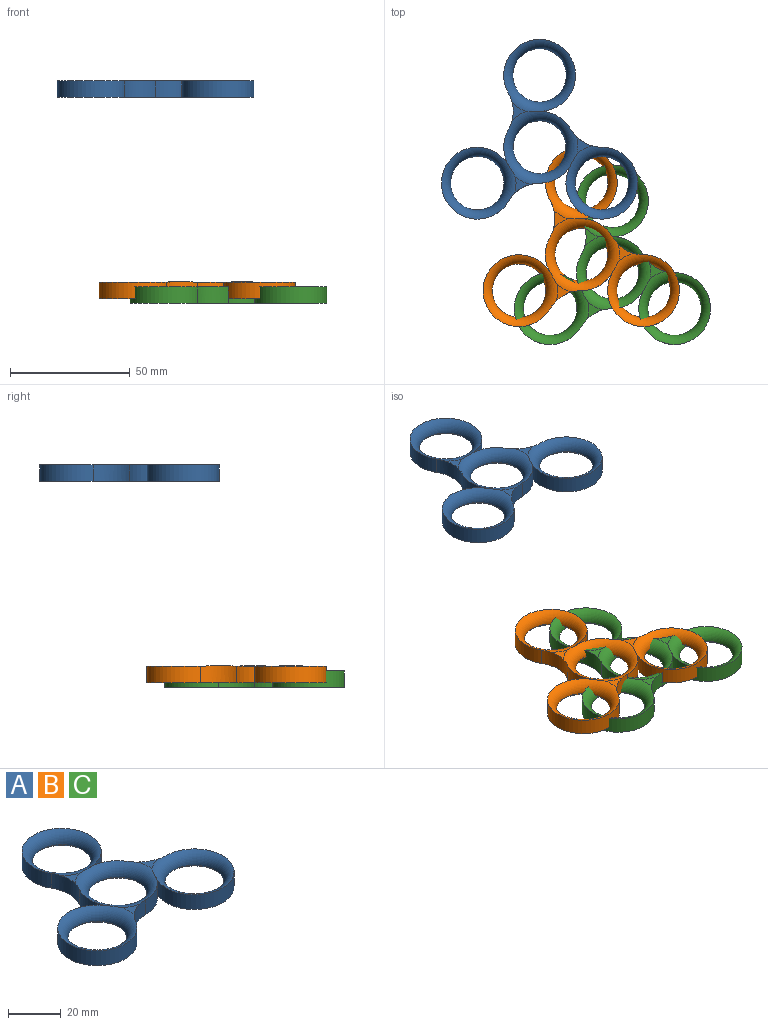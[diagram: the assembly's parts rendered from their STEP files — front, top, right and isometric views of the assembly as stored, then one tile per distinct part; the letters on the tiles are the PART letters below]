
ASSEMBLY  parts=3 mates=1
PART A: 23 faces, bbox 94.6x87.6x8.6 mm
  f0: plane 12.47x12.17mm, normal (0,0,-1), area 34.2mm2, adj f8,f19,f22
  f1: plane 13.66x11.49mm, normal (0,0,-1), area 34.2mm2, adj f11,f20,f22
  f2: plane 6.71x6.48mm, normal (0,0,1), area 15.5mm2, adj f8,f16,f21
  f3: plane 7.43x5.71mm, normal (0,0,1), area 15.5mm2, adj f5,f15,f21
  f4: cylinder r=15mm len=30mm, axis (0,0,-1), area 539.1mm2, adj f5,f12,f15,f18
  f5: cylinder r=15mm len=15mm, axis (0,0,-1), area 109.5mm2, adj f3,f4,f6,f14,f15,f18,f21
  f6: cylinder r=15mm len=15mm, axis (0,0,-1), area 108.3mm2, adj f5,f7,f16,f19,f21,f22
  f7: cylinder r=15mm len=30mm, axis (0,0,-1), area 539.1mm2, adj f6,f8,f16,f19
  f8: cylinder r=15mm len=12.99mm, axis (0,0,-1), area 109.5mm2, adj f0,f2,f7,f9,f16,f19,f21
  f9: cylinder r=15mm len=12.99mm, axis (0,0,-1), area 108.3mm2, adj f8,f10,f17,f20,f21,f22
  f10: cylinder r=15mm len=30mm, axis (0,0,-1), area 539.1mm2, adj f9,f11,f17,f20
  f11: cylinder r=15mm len=12.99mm, axis (0,0,-1), area 109.5mm2, adj f1,f10,f12,f13,f17,f20,f21
  f12: cylinder r=15mm len=12.99mm, axis (0,0,-1), area 108.3mm2, adj f4,f11,f15,f18,f21,f22
  f13: plane 6.83x6.4mm, normal (0,0,1), area 15.5mm2, adj f11,f17,f21
  f14: plane 13.66x11.49mm, normal (0,0,-1), area 34.2mm2, adj f5,f18,f22
  f15: torus R=16.15mm, axis (0,0,1), area 537.9mm2, adj f3,f4,f5,f12,f18,f21
  f16: torus R=16.15mm, axis (0,0,1), area 537.9mm2, adj f2,f6,f7,f8,f19,f21
  f17: torus R=16.15mm, axis (0,0,1), area 537.9mm2, adj f9,f10,f11,f13,f20,f21
  f18: torus R=15.15mm, axis (0,0,1), area 366.5mm2, adj f4,f5,f12,f14,f15,f22
  f19: torus R=15.15mm, axis (0,0,1), area 366.5mm2, adj f0,f6,f7,f8,f16,f22
  f20: torus R=15.15mm, axis (0,0,1), area 366.5mm2, adj f1,f9,f10,f11,f17,f22
  f21: torus R=16mm, axis (0,0,1), area 562.8mm2, adj f2,f3,f5,f6,f8,f9,f11,f12
  f22: torus R=15mm, axis (0,0,1), area 373.7mm2, adj f0,f1,f6,f9,f12,f14,f18,f19
PART B: same geometry as A
PART C: same geometry as A
PLACE A t=(-42.6,69.47,139.25)mm
PLACE B rot(axis=(0.5,0.68,0.53),0deg) t=(-25.21,24.76,55.25)mm
PLACE C rot(axis=(0.5,0.68,0.53),0deg) t=(-12.22,17.26,53.25)mm
MATE fastened C.f6 <-> B.f1  axis (0,0,1) through (-12.22,17.26,55.25)mm
